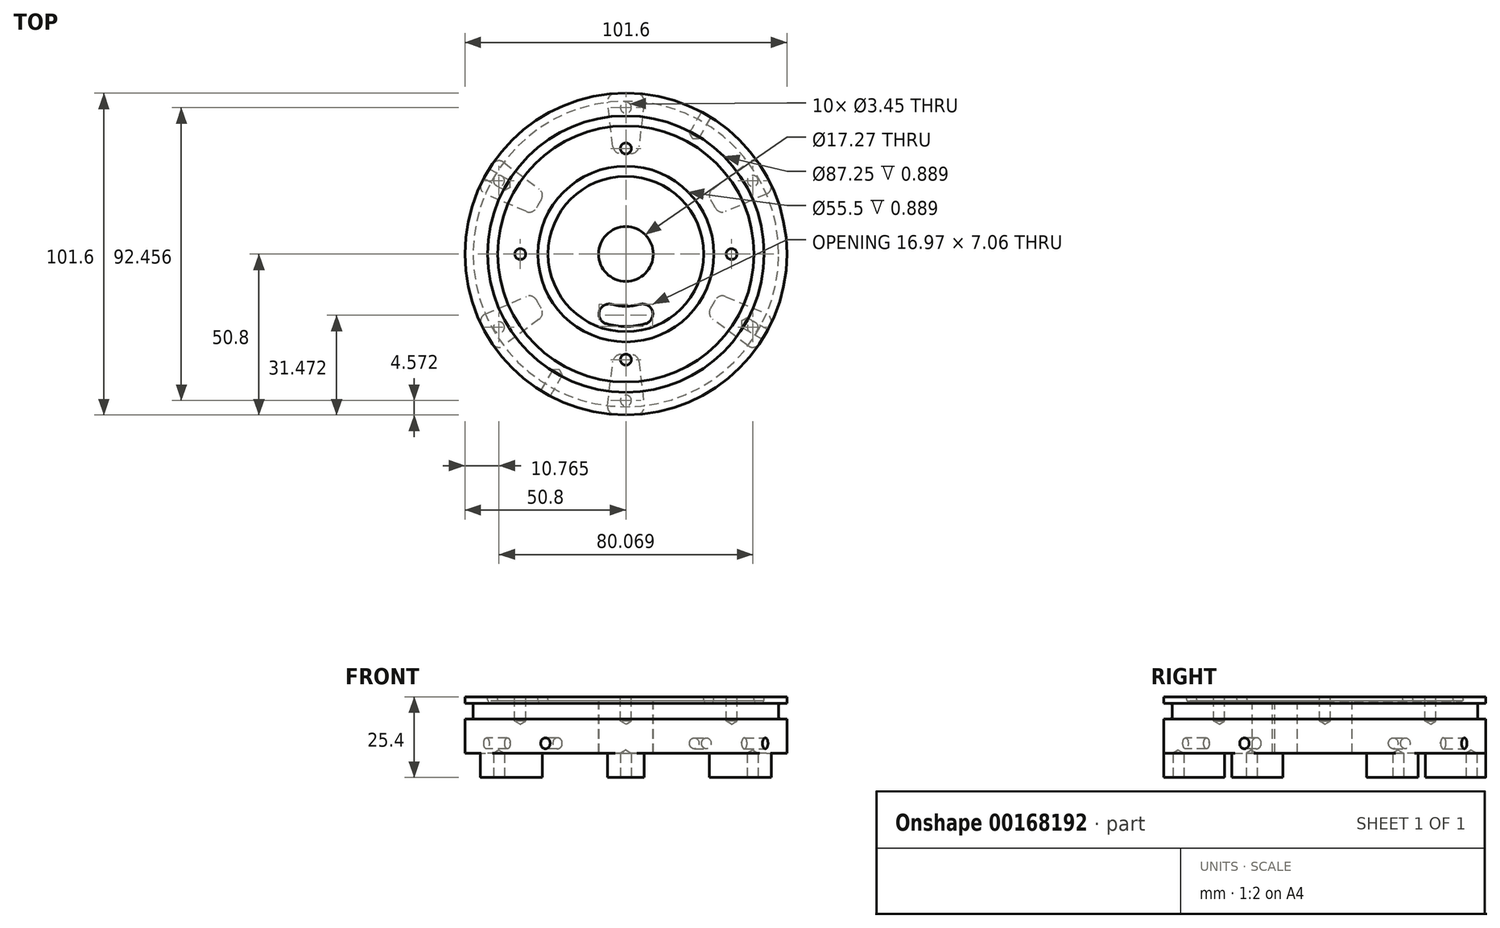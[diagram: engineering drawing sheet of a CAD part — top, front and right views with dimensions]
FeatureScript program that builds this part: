
annotation { "Feature Type Name" : "Feature", "Feature Type Description" : "" }
export const myFeature = defineFeature(function(context is Context, id is Id, definition is map)
    precondition{}
    {
        {
            var Q0;
            Q0=qCreatedBy(makeId("Top.planeOp"),FACE);
            var sketch = newSketch(context, id + "F0", { "sketchPlane" : qUnion([Q0])});
            skCircle(sketch, "E0", {"center": v(0, 0) * mm, "radius": 50.8 * mm});
            skSolve(sketch);
        }
        {
            var Q0;
            Q0=makeQuery(id+"F0.imprint","IMPRINT",FACE,{"disambiguationData":[TD([[makeQuery(id+"F0.imprint","IMPRINT",EDGE,{"derivedFrom":sQuery(id+"F0.wireOp",EDGE,"E0")}),1.0]])]});
            extrude(context, id + "F1", {"entities" : qUnion([Q0]), "depth" : 17.78 * mm});
        }
        {
            var Q0;
            Q0=makeQuery(id+"FNZgXB3MDCEPfWC_1.boolean.opBoolean","SPLIT",FACE,{"disambiguationData":[TD([makeQuery(id+"FNZgXB3MDCEPfWC_1.opExtrude","SWEPT_FACE",FACE,{"disambiguationData":[OSD([sQuery(id+"FiLk9hSRQ8Dv81E_1.wireOp",EDGE,"Xvq2NHEn-EDZK-GzOR-rNrk-moL4fFsD4KvI")])]})])],"derivedFrom":makeQuery(id+"F1.opExtrude","CAP_FACE",FACE,{"disambiguationData":[OSD([sQuery(id+"F0.wireOp",EDGE,"E0")])],"isStart":false})});
            var sketch = newSketch(context, id + "F2", { "sketchPlane" : qUnion([Q0])});
            skCircle(sketch, "E1", {"center": v(0, 0) * mm, "radius": 8.64 * mm});
            skSolve(sketch);
        }
        {
            var Q0;
            Q0=qSketchRegion(id+"F2",true);
            extrude(context, id + "F3", {"entities" : qUnion([Q0]), "operationType" : NewBodyOperationType.REMOVE, "endBound" : BoundingType.THROUGH_ALL, "oppositeDirection" : true, "depth" : 25.4 * mm});
        }
        {
            var Q0;
            Q0=makeQuery(id+"F1.opExtrude","CAP_FACE",FACE,{"disambiguationData":[OSD([sQuery(id+"F0.wireOp",EDGE,"E0")])],"isStart":true});
            var sketch = newSketch(context, id + "F4", { "sketchPlane" : qUnion([Q0])});
            skArc(sketch, "E2", {"start": v(-6.1, -50.43) * mm, "mid": v(0, -50.8) * mm, "end": v(6.1, -50.43) * mm});
            skArc(sketch, "E3", {"start": v(-3.81, -31.52) * mm, "mid": v(0, -31.75) * mm, "end": v(3.8, -31.52) * mm});
            skLineSegment(sketch, "E4", {"start": v(0, 0) * mm, "end": v(3.81, -31.52) * mm, "construction": true});
            skLineSegment(sketch, "E5", {"start": v(6.1, -50.43) * mm, "end": v(3.8, -31.52) * mm});
            skLineSegment(sketch, "E6", {"start": v(-3.8, -31.52) * mm, "end": v(-6.1, -50.43) * mm});
            skLineSegment(sketch, "E7", {"start": v(-3.81, -31.52) * mm, "end": v(3.81, -31.52) * mm, "construction": true});
            skPoint(sketch, "E8", {"position": v(0, -31.52) * mm});
            skLineSegment(sketch, "E9", {"start": v(0, 0) * mm, "end": v(-3.81, -31.52) * mm, "construction": true});
            skSolve(sketch);
        }
        {
            var Q0;
            Q0=qSketchRegion(id+"F4",true);
            extrude(context, id + "F5", {"entities" : qUnion([Q0]), "operationType" : NewBodyOperationType.ADD, "depth" : 7.62 * mm});
        }
        {
            var Q0;
            Q0=makeQuery(id+"F5.opExtrude","SWEPT_EDGE",EDGE,{"disambiguationData":[OSD([sQuery(id+"F0.wireOp",EDGE,"E0"),sQuery(id+"F4.wireOp",EDGE,"E2"),sQuery(id+"F4.wireOp",EDGE,"E5")])]});
            var Q1;
            Q1=makeQuery(id+"F5.opExtrude","SWEPT_EDGE",EDGE,{"disambiguationData":[OSD([sQuery(id+"F4.wireOp",EDGE,"E3"),sQuery(id+"F4.wireOp",EDGE,"E5")])]});
            var Q2;
            Q2=makeQuery(id+"F5.opExtrude","SWEPT_EDGE",EDGE,{"disambiguationData":[OSD([sQuery(id+"F0.wireOp",EDGE,"E0"),sQuery(id+"F4.wireOp",EDGE,"E2"),sQuery(id+"F4.wireOp",EDGE,"sxsrdx0H-xiQs-OsdF-6Z6r-2XBd8uqwUAgb")])]});
            var Q3;
            Q3=makeQuery(id+"F5.opExtrude","SWEPT_EDGE",EDGE,{"disambiguationData":[OSD([sQuery(id+"F4.wireOp",EDGE,"E3"),sQuery(id+"F4.wireOp",EDGE,"sxsrdx0H-xiQs-OsdF-6Z6r-2XBd8uqwUAgb")])]});
            fillet(context, id + "F6", {"entities" : qUnion([Q0, Q1, Q2, Q3]), "radius" : 2.54 * mm, "tangentPropagation" : true, "allowEdgeOverflow" : false});
        }
        {
            var Q0;
            Q0=makeQuery(id+"F5.opExtrude","CAP_FACE",FACE,{"disambiguationData":[OSD([sQuery(id+"F4.wireOp",EDGE,"E2"),sQuery(id+"F4.wireOp",EDGE,"E3"),sQuery(id+"F4.wireOp",EDGE,"E5"),sQuery(id+"F4.wireOp",EDGE,"sxsrdx0H-xiQs-OsdF-6Z6r-2XBd8uqwUAgb")])],"isStart":false});
            var sketch = newSketch(context, id + "F7", { "sketchPlane" : qUnion([Q0])});
            skLineSegment(sketch, "E10", {"start": v(0, 0) * mm, "end": v(0, 0) * mm});
            skLineSegment(sketch, "E11", {"start": v(0, 0) * mm, "end": v(0, -50.68) * mm, "construction": true});
            skPoint(sketch, "E12.3.0", {"position": v(0, -46.23) * mm});
            skPoint(sketch, "E12.center", {"position": v(0, 0) * mm});
            skPoint(sketch, "E13.1.0", {"position": v(40.03, -23.11) * mm});
            skPoint(sketch, "E13.2.0", {"position": v(40.03, 23.11) * mm});
            skPoint(sketch, "E14.0.3.0", {"position": v(0, 46.23) * mm});
            skPoint(sketch, "E14.0.4.0", {"position": v(-40.03, 23.11) * mm});
            skPoint(sketch, "E14.0.5.0", {"position": v(-40.03, -23.11) * mm});
            skSolve(sketch);
        }
        {
            var Q0;
            Q0=makeQuery(id+"F1.opExtrude","SWEPT_BODY",BODY,{"disambiguationData":[OSD([sQuery(id+"F0.wireOp",EDGE,"E0")])]});
            var Q1;
            Q1=makeQuery(id+"F3.boolean.opBoolean","COPY",FACE,{"derivedFrom":makeQuery(id+"F3.opExtrude","SWEPT_FACE",FACE,{"disambiguationData":[OSD([sQuery(id+"F2.wireOp",EDGE,"E1")])]})});
            circularPattern(context, id + "F8", {"operationType" : NewBodyOperationType.ADD, "entities" : qUnion([Q0]), "axis" : qUnion([Q1]), "angle" : 360 * degree, "instanceCount" : 6, "equalSpace" : true});
        }
        {
            var Q0;
            Q0=sQuery(id+"F7.wireOp",VERTEX,"E12.3.0");
            var Q1;
            Q1=sQuery(id+"F7.wireOp",VERTEX,"E13.1.0");
            var Q2;
            Q2=sQuery(id+"F7.wireOp",VERTEX,"E13.2.0");
            var Q3;
            Q3=sQuery(id+"F7.wireOp",VERTEX,"E14.0.3.0");
            var Q4;
            Q4=sQuery(id+"F7.wireOp",VERTEX,"E14.0.4.0");
            var Q5;
            Q5=sQuery(id+"F7.wireOp",VERTEX,"E14.0.5.0");
            var Q6;
            Q6=makeQuery(id+"F1.opExtrude","SWEPT_BODY",BODY,{"disambiguationData":[OSD([sQuery(id+"F0.wireOp",EDGE,"E0")])]});
            hole(context, id + "F9", {"style" : HoleStyle.SIMPLE, "endStyle" : HoleEndStyle.BLIND, "standardTappedOrClearance" : lookupTablePath({ "standard" : "ANSI", "engagement" : "75%", "pitch" : "32 tpi", "size" : "#8", "type" : "Tapped" }), "standardBlindInLast" : lookupTablePath({ "standard" : "ANSI", "engagement" : "75%", "pitch" : "32 tpi", "size" : "#8", "type" : "Tapped" }), "holeDiameter" : 3.45 * mm, "holeDepth" : 7.62 * mm, "locations" : qUnion([Q0, Q1, Q2, Q3, Q4, Q5]), "scope" : qUnion([Q6]), "majorDiameter" : 4.17 * mm});
        }
        {
            var Q0;
            {var subQ0=sQuery(id+"F0.wireOp",EDGE,"E0");Q0=makeQuery(id+"FNZgXB3MDCEPfWC_1.boolean.opBoolean","SPLIT",FACE,{"disambiguationData":[TD([makeQuery(id+"F1.opExtrude","SWEPT_FACE",FACE,{"disambiguationData":[OSD([subQ0])]})])],"derivedFrom":makeQuery(id+"F1.opExtrude","CAP_FACE",FACE,{"disambiguationData":[OSD([subQ0])],"isStart":false})});}
            var sketch = newSketch(context, id + "F10", { "sketchPlane" : qUnion([Q0])});
            skCircle(sketch, "E15", {"center": v(0, 0) * mm, "radius": 42.02 * mm, "construction": true});
            skCircle(sketch, "E16", {"center": v(0, 0) * mm, "radius": 40.42 * mm});
            skCircle(sketch, "E17", {"center": v(0, 0) * mm, "radius": 43.62 * mm});
            skSolve(sketch);
        }
        {
            var Q0;
            Q0=qSketchRegion(id+"F10",true);
            extrude(context, id + "F11", {"entities" : qUnion([Q0]), "operationType" : NewBodyOperationType.REMOVE, "oppositeDirection" : true, "depth" : 1.3 * mm});
        }
        {
            var Q0;
            Q0=makeQuery(id+"F11.boolean.opBoolean","COPY",EDGE,{"derivedFrom":makeQuery(id+"F11.opExtrude","CAP_EDGE",EDGE,{"disambiguationData":[OSD([sQuery(id+"F10.wireOp",EDGE,"E17")])],"isStart":false})});
            var Q1;
            Q1=makeQuery(id+"F11.boolean.opBoolean","COPY",EDGE,{"derivedFrom":makeQuery(id+"F11.opExtrude","CAP_EDGE",EDGE,{"disambiguationData":[OSD([sQuery(id+"F10.wireOp",EDGE,"E16")])],"isStart":false})});
            fillet(context, id + "F12", {"entities" : qUnion([Q0, Q1]), "radius" : 0.4 * mm, "tangentPropagation" : true, "allowEdgeOverflow" : false});
        }
        {
            var Q0;
            Q0=makeQuery(id+"F11.boolean.opBoolean","SPLIT",FACE,{"disambiguationData":[TD([makeQuery(id+"F3.boolean.opBoolean","COPY",FACE,{"derivedFrom":makeQuery(id+"F3.opExtrude","SWEPT_FACE",FACE,{"disambiguationData":[OSD([sQuery(id+"F2.wireOp",EDGE,"E1")])]})})])],"derivedFrom":makeQuery(id+"F1.opExtrude","CAP_FACE",FACE,{"disambiguationData":[OSD([sQuery(id+"F0.wireOp",EDGE,"E0")])],"isStart":false})});
            var sketch = newSketch(context, id + "F13", { "sketchPlane" : qUnion([Q0])});
            skCircle(sketch, "E18", {"center": v(0, 0) * mm, "radius": 26.15 * mm, "construction": true});
            skCircle(sketch, "E19", {"center": v(0, 0) * mm, "radius": 24.55 * mm});
            skCircle(sketch, "E20", {"center": v(0, 0) * mm, "radius": 27.75 * mm});
            skSolve(sketch);
        }
        {
            var Q0;
            Q0=qSketchRegion(id+"F13",true);
            extrude(context, id + "F14", {"entities" : qUnion([Q0]), "operationType" : NewBodyOperationType.REMOVE, "oppositeDirection" : true, "depth" : 1.3 * mm});
        }
        {
            var Q0;
            Q0=makeQuery(id+"F14.boolean.opBoolean","COPY",EDGE,{"derivedFrom":makeQuery(id+"F14.opExtrude","CAP_EDGE",EDGE,{"disambiguationData":[OSD([sQuery(id+"F13.wireOp",EDGE,"E20")])],"isStart":false})});
            var Q1;
            Q1=makeQuery(id+"F14.boolean.opBoolean","COPY",EDGE,{"derivedFrom":makeQuery(id+"F14.opExtrude","CAP_EDGE",EDGE,{"disambiguationData":[OSD([sQuery(id+"F13.wireOp",EDGE,"E19")])],"isStart":false})});
            fillet(context, id + "F15", {"entities" : qUnion([Q0, Q1]), "radius" : 0.4 * mm, "tangentPropagation" : true, "allowEdgeOverflow" : false});
        }
        {
            var Q0;
            {var subQ0=makeQuery(id+"F3.boolean.opBoolean","COPY",FACE,{"derivedFrom":makeQuery(id+"F3.opExtrude","SWEPT_FACE",FACE,{"disambiguationData":[OSD([sQuery(id+"F2.wireOp",EDGE,"E1")])]})});Q0=makeQuery(id+"F14.boolean.opBoolean","SPLIT",FACE,{"disambiguationData":[TD([subQ0])],"derivedFrom":makeQuery(id+"F11.boolean.opBoolean","SPLIT",FACE,{"disambiguationData":[TD([subQ0])],"derivedFrom":makeQuery(id+"F1.opExtrude","CAP_FACE",FACE,{"disambiguationData":[OSD([sQuery(id+"F0.wireOp",EDGE,"E0")])],"isStart":false})})});}
            var sketch = newSketch(context, id + "F16", { "sketchPlane" : qUnion([Q0])});
            skLineSegment(sketch, "E21", {"start": v(0, 0) * mm, "end": v(6.98, -14.96) * mm, "construction": true});
            skArc(sketch, "E22", {"start": v(6.98, -14.96) * mm, "mid": v(0, -16.51) * mm, "end": v(-6.98, -14.96) * mm});
            skArc(sketch, "E23", {"start": v(9.66, -20.72) * mm, "mid": v(0, -22.86) * mm, "end": v(-9.66, -20.72) * mm});
            skLineSegment(sketch, "E24", {"start": v(-9.66, -20.72) * mm, "end": v(-6.98, -14.96) * mm});
            skLineSegment(sketch, "E25", {"start": v(0, 0) * mm, "end": v(-6.98, -14.96) * mm, "construction": true});
            skLineSegment(sketch, "E26", {"start": v(9.66, -20.72) * mm, "end": v(6.98, -14.96) * mm});
            skLineSegment(sketch, "E27", {"start": v(0, -16.51) * mm, "end": v(0, 0) * mm, "construction": true});
            skSolve(sketch);
        }
        {
            var Q0;
            Q0=qSketchRegion(id+"F16",true);
            extrude(context, id + "F17", {"entities" : qUnion([Q0]), "operationType" : NewBodyOperationType.REMOVE, "endBound" : BoundingType.THROUGH_ALL, "oppositeDirection" : true, "depth" : 25.4 * mm});
        }
        {
            var Q0;
            Q0=makeQuery(id+"F17.boolean.opBoolean","COPY",EDGE,{"derivedFrom":makeQuery(id+"F17.opExtrude","SWEPT_EDGE",EDGE,{"disambiguationData":[OSD([sQuery(id+"F16.wireOp",EDGE,"E22"),sQuery(id+"F16.wireOp",EDGE,"E24")])]})});
            var Q1;
            Q1=makeQuery(id+"F17.boolean.opBoolean","COPY",EDGE,{"derivedFrom":makeQuery(id+"F17.opExtrude","SWEPT_EDGE",EDGE,{"disambiguationData":[OSD([sQuery(id+"F16.wireOp",EDGE,"E23"),sQuery(id+"F16.wireOp",EDGE,"E24")])]})});
            var Q2;
            Q2=makeQuery(id+"F17.boolean.opBoolean","COPY",EDGE,{"derivedFrom":makeQuery(id+"F17.opExtrude","SWEPT_EDGE",EDGE,{"disambiguationData":[OSD([sQuery(id+"F16.wireOp",EDGE,"E22"),sQuery(id+"F16.wireOp",EDGE,"nJm0js4g-YAOA-XNub-Ppl5-B8IrQimasCNu")])]})});
            var Q3;
            Q3=makeQuery(id+"F17.boolean.opBoolean","COPY",EDGE,{"derivedFrom":makeQuery(id+"F17.opExtrude","SWEPT_EDGE",EDGE,{"disambiguationData":[OSD([sQuery(id+"F16.wireOp",EDGE,"E23"),sQuery(id+"F16.wireOp",EDGE,"nJm0js4g-YAOA-XNub-Ppl5-B8IrQimasCNu")])]})});
            fillet(context, id + "F18", {"entities" : qUnion([Q0, Q1, Q2, Q3]), "radius" : 3.17 * mm, "tangentPropagation" : true, "allowEdgeOverflow" : false});
        }
        {
            var Q0;
            {var subQ0=makeQuery(id+"F11.opExtrude","SWEPT_FACE",FACE,{"disambiguationData":[OSD([sQuery(id+"F10.wireOp",EDGE,"E16")])]});Q0=makeQuery(id+"F14.boolean.opBoolean","SPLIT",FACE,{"disambiguationData":[TD([makeQuery(id+"F11.boolean.opBoolean","COPY",FACE,{"derivedFrom":subQ0})])],"derivedFrom":makeQuery(id+"F11.boolean.opBoolean","SPLIT",FACE,{"disambiguationData":[TD([makeQuery(id+"F3.boolean.opBoolean","COPY",FACE,{"derivedFrom":makeQuery(id+"F3.opExtrude","SWEPT_FACE",FACE,{"disambiguationData":[OSD([sQuery(id+"F2.wireOp",EDGE,"E1")])]})})])],"derivedFrom":makeQuery(id+"F1.opExtrude","CAP_FACE",FACE,{"disambiguationData":[OSD([sQuery(id+"F0.wireOp",EDGE,"E0")])],"isStart":false})})});}
            var sketch = newSketch(context, id + "F19", { "sketchPlane" : qUnion([Q0])});
            skCircle(sketch, "E28", {"center": v(0, 0) * mm, "radius": 33.34 * mm, "construction": true});
            skLineSegment(sketch, "E29", {"start": v(0, 0) * mm, "end": v(0, -33.34) * mm, "construction": true});
            skPoint(sketch, "E30", {"position": v(0, -33.34) * mm});
            skPoint(sketch, "E31", {"position": v(-33.34, 0) * mm});
            skPoint(sketch, "E32", {"position": v(33.34, 0) * mm});
            skPoint(sketch, "E33", {"position": v(0, 33.34) * mm});
            skSolve(sketch);
        }
        {
            var Q0;
            {var subQ1=sQuery(id+"F0.wireOp",EDGE,"E0");var subQ2=makeQuery(id+"F1.opExtrude","SWEPT_FACE",FACE,{"disambiguationData":[OSD([subQ1])]});Q0=makeQuery(id+"F11.boolean.opBoolean","SPLIT",FACE,{"disambiguationData":[TD([subQ2])],"derivedFrom":makeQuery(id+"F1.opExtrude","CAP_FACE",FACE,{"disambiguationData":[OSD([subQ1])],"isStart":false})});}
            cPlane(context, id + "F20", {"entities" : qUnion([Q0]), "cplaneType" : CPlaneType.OFFSET, "offset" : 2.03 * mm, "oppositeDirection" : true, "width" : 152.4 * mm, "height" : 152.4 * mm});
        }
        {
            var Q0;
            Q0=qCreatedBy(id+"F20.planeOp",FACE);
            var sketch = newSketch(context, id + "F21", { "sketchPlane" : qUnion([Q0])});
            skCircle(sketch, "E34", {"center": v(0, 0) * mm, "radius": 48.2 * mm});
            skCircle(sketch, "E35.0", {"center": v(0, 0) * mm, "radius": 50.8 * mm});
            skSolve(sketch);
        }
        {
            var Q0;
            Q0=qSketchRegion(id+"F21",true);
            extrude(context, id + "F22", {"entities" : qUnion([Q0]), "operationType" : NewBodyOperationType.REMOVE, "oppositeDirection" : true, "depth" : 5 * mm});
        }
        {
            var Q0;
            Q0=makeQuery(id+"F22.boolean.opBoolean","COPY",EDGE,{"derivedFrom":makeQuery(id+"F22.opExtrude","CAP_EDGE",EDGE,{"disambiguationData":[OSD([sQuery(id+"F21.wireOp",EDGE,"E34")])],"isStart":false})});
            var Q1;
            Q1=makeQuery(id+"F22.boolean.opBoolean","COPY",EDGE,{"derivedFrom":makeQuery(id+"F22.opExtrude","CAP_EDGE",EDGE,{"disambiguationData":[OSD([sQuery(id+"F21.wireOp",EDGE,"E34")])],"isStart":true})});
            fillet(context, id + "F23", {"entities" : qUnion([Q0, Q1]), "radius" : 0.76 * mm, "tangentPropagation" : true, "allowEdgeOverflow" : false});
        }
        {
            var Q0;
            {var subQ1=sQuery(id+"F0.wireOp",EDGE,"E0");var subQ2=makeQuery(id+"F1.opExtrude","SWEPT_FACE",FACE,{"disambiguationData":[OSD([subQ1])]});Q0=makeQuery(id+"F11.boolean.opBoolean","SPLIT",FACE,{"disambiguationData":[TD([subQ2])],"derivedFrom":makeQuery(id+"F1.opExtrude","CAP_FACE",FACE,{"disambiguationData":[OSD([subQ1])],"isStart":false})});}
            var sketch = newSketch(context, id + "F24", { "sketchPlane" : qUnion([Q0])});
            skCircle(sketch, "E36.0", {"center": v(0, 0) * mm, "radius": 50.8 * mm, "construction": true});
            skPoint(sketch, "E37", {"position": v(-25.4, -44) * mm});
            skLineSegment(sketch, "E38", {"start": v(0, -50.8) * mm, "end": v(0, 0) * mm, "construction": true});
            skLineSegment(sketch, "E39", {"start": v(0, 0) * mm, "end": v(-17.96, -31.1) * mm, "construction": true});
            skLineSegment(sketch, "E40", {"start": v(-17.96, -31.1) * mm, "end": v(-25.4, -44) * mm, "construction": true});
            skLineSegment(sketch, "E41", {"start": v(0, 0) * mm, "end": v(25.4, 44) * mm, "construction": true});
            skLineSegment(sketch, "E42", {"start": v(25.4, 44) * mm, "end": v(0, 0) * mm, "construction": true});
            skLineSegment(sketch, "E43", {"start": v(44, -25.4) * mm, "end": v(0, 0) * mm, "construction": true});
            skLineSegment(sketch, "E44", {"start": v(0, 0) * mm, "end": v(-44, 25.4) * mm, "construction": true});
            skPoint(sketch, "E45", {"position": v(25.4, 44) * mm});
            skPoint(sketch, "E46", {"position": v(44, -25.4) * mm});
            skPoint(sketch, "E47", {"position": v(-44, 25.4) * mm});
            skSolve(sketch);
        }
        {
            var Q0;
            Q0=qCreatedBy(makeId("Front.planeOp"),FACE);
            var sketch = newSketch(context, id + "F25", { "sketchPlane" : qUnion([Q0])});
            skLineSegment(sketch, "E48", {"start": v(0, 0) * mm, "end": v(0, 38.57) * mm, "construction": true});
            skSolve(sketch);
        }
        {
            var Q0;
            Q0=sQuery(id+"F25.wireOp",EDGE,"E48");
            cPlane(context, id + "F26", {"entities" : qUnion([Q0]), "cplaneType" : CPlaneType.LINE_ANGLE, "offset" : 25.4 * mm, "angle" : 60 * degree, "width" : 152.4 * mm, "height" : 152.4 * mm});
        }
        {
            var Q0;
            Q0=sQuery(id+"F24.wireOp",VERTEX,"E37");
            var Q1;
            Q1=qCreatedBy(id+"F26.planeOp",FACE);
            cPlane(context, id + "F27", {"entities" : qUnion([Q0, Q1]), "cplaneType" : CPlaneType.PLANE_POINT, "offset" : 25.4 * mm, "width" : 152.4 * mm, "height" : 152.4 * mm});
        }
        {
            var Q0;
            Q0=qCreatedBy(id+"F27.planeOp",FACE);
            var Q1;
            Q1=sQuery(id+"F24.wireOp",VERTEX,"E45");
            cPlane(context, id + "F28", {"entities" : qUnion([Q0, Q1]), "cplaneType" : CPlaneType.PLANE_POINT, "offset" : 25.4 * mm, "width" : 152.4 * mm, "height" : 152.4 * mm});
        }
        {
            var Q0;
            Q0=sQuery(id+"F25.wireOp",EDGE,"E48");
            cPlane(context, id + "F29", {"entities" : qUnion([Q0]), "cplaneType" : CPlaneType.LINE_ANGLE, "offset" : 25.4 * mm, "angle" : 150 * degree, "width" : 152.4 * mm, "height" : 152.4 * mm});
        }
        {
            var Q0;
            Q0=sQuery(id+"F24.wireOp",VERTEX,"E47");
            var Q1;
            Q1=qCreatedBy(id+"F29.planeOp",FACE);
            cPlane(context, id + "F30", {"entities" : qUnion([Q0, Q1]), "cplaneType" : CPlaneType.PLANE_POINT, "offset" : 25.4 * mm, "width" : 152.4 * mm, "height" : 152.4 * mm});
        }
        {
            var Q0;
            Q0=qCreatedBy(id+"F29.planeOp",FACE);
            var Q1;
            Q1=sQuery(id+"F24.wireOp",VERTEX,"E46");
            cPlane(context, id + "F31", {"entities" : qUnion([Q0, Q1]), "cplaneType" : CPlaneType.PLANE_POINT, "offset" : 25.4 * mm, "width" : 152.4 * mm, "height" : 152.4 * mm});
        }
        {
            var Q0;
            Q0=qCreatedBy(id+"F27.planeOp",FACE);
            var sketch = newSketch(context, id + "F32", { "sketchPlane" : qUnion([Q0])});
            skLineSegment(sketch, "E49", {"start": v(0, 0) * mm, "end": v(0, 3.12) * mm, "construction": true});
            skPoint(sketch, "E50", {"position": v(0, 3.12) * mm});
            skSolve(sketch);
        }
        {
            var Q0;
            Q0=qCreatedBy(id+"F28.planeOp",FACE);
            var sketch = newSketch(context, id + "F33", { "sketchPlane" : qUnion([Q0])});
            skPoint(sketch, "E51", {"position": v(0, 3.12) * mm});
            skLineSegment(sketch, "E52.0", {"start": v(0, 0) * mm, "end": v(0, 3.12) * mm, "construction": true});
            skSolve(sketch);
        }
        {
            var Q0;
            Q0=qCreatedBy(id+"F30.planeOp",FACE);
            var sketch = newSketch(context, id + "F34", { "sketchPlane" : qUnion([Q0])});
            skLineSegment(sketch, "E53", {"start": v(0, 0) * mm, "end": v(0, 3.12) * mm, "construction": true});
            skLineSegment(sketch, "E54.0", {"start": v(-50.8, 0) * mm, "end": v(-50.8, 3.12) * mm, "construction": true});
            skPoint(sketch, "E55", {"position": v(0, 3.12) * mm});
            skLineSegment(sketch, "E56", {"start": v(-50.8, 3.12) * mm, "end": v(0, 3.12) * mm, "construction": true});
            skSolve(sketch);
        }
        {
            var Q0;
            Q0=qCreatedBy(id+"F31.planeOp",FACE);
            var sketch = newSketch(context, id + "F35", { "sketchPlane" : qUnion([Q0])});
            skLineSegment(sketch, "E57.0", {"start": v(0, 0) * mm, "end": v(0, 3.12) * mm, "construction": true});
            skPoint(sketch, "E58", {"position": v(0, 3.12) * mm});
            skSolve(sketch);
        }
        {
            var Q0;
            Q0=sQuery(id+"F35.wireOp",VERTEX,"E58");
            var Q1;
            Q1=makeQuery(id+"F1.opExtrude","SWEPT_BODY",BODY,{"disambiguationData":[OSD([sQuery(id+"F0.wireOp",EDGE,"E0")])]});
            hole(context, id + "F36", {"style" : HoleStyle.SIMPLE, "endStyle" : HoleEndStyle.BLIND, "oppositeDirection" : true, "standardTappedOrClearance" : lookupTablePath({ "standard" : "ANSI", "engagement" : "75%", "pitch" : "32 tpi", "size" : "#8", "type" : "Tapped" }), "standardBlindInLast" : lookupTablePath({ "standard" : "ANSI", "engagement" : "75%", "pitch" : "32 tpi", "size" : "#8", "type" : "Tapped" }), "holeDiameter" : 3.45 * mm, "holeDepth" : 7.62 * mm, "locations" : qUnion([Q0]), "scope" : qUnion([Q1]), "majorDiameter" : 4.17 * mm});
        }
        {
            var Q0;
            Q0=sQuery(id+"F34.wireOp",VERTEX,"E55");
            var Q1;
            Q1=makeQuery(id+"F1.opExtrude","SWEPT_BODY",BODY,{"disambiguationData":[OSD([sQuery(id+"F0.wireOp",EDGE,"E0")])]});
            hole(context, id + "F37", {"style" : HoleStyle.SIMPLE, "endStyle" : HoleEndStyle.BLIND, "standardTappedOrClearance" : lookupTablePath({ "standard" : "ANSI", "engagement" : "75%", "pitch" : "32 tpi", "size" : "#8", "type" : "Tapped" }), "standardBlindInLast" : lookupTablePath({ "standard" : "ANSI", "engagement" : "75%", "pitch" : "32 tpi", "size" : "#8", "type" : "Tapped" }), "holeDiameter" : 3.45 * mm, "holeDepth" : 7.62 * mm, "locations" : qUnion([Q0]), "scope" : qUnion([Q1]), "majorDiameter" : 4.17 * mm});
        }
        {
            var Q0;
            Q0=sQuery(id+"F32.wireOp",VERTEX,"E50");
            var Q1;
            Q1=makeQuery(id+"F1.opExtrude","SWEPT_BODY",BODY,{"disambiguationData":[OSD([sQuery(id+"F0.wireOp",EDGE,"E0")])]});
            hole(context, id + "F38", {"style" : HoleStyle.SIMPLE, "endStyle" : HoleEndStyle.BLIND, "oppositeDirection" : true, "standardTappedOrClearance" : lookupTablePath({ "standard" : "ANSI", "engagement" : "75%", "pitch" : "32 tpi", "size" : "#8", "type" : "Tapped" }), "standardBlindInLast" : lookupTablePath({ "standard" : "ANSI", "engagement" : "75%", "pitch" : "32 tpi", "size" : "#8", "type" : "Tapped" }), "holeDiameter" : 3.45 * mm, "holeDepth" : 7.62 * mm, "locations" : qUnion([Q0]), "scope" : qUnion([Q1]), "majorDiameter" : 4.17 * mm});
        }
        {
            var Q0;
            Q0=sQuery(id+"F33.wireOp",VERTEX,"E51");
            var Q1;
            Q1=makeQuery(id+"F1.opExtrude","SWEPT_BODY",BODY,{"disambiguationData":[OSD([sQuery(id+"F0.wireOp",EDGE,"E0")])]});
            hole(context, id + "F39", {"style" : HoleStyle.SIMPLE, "endStyle" : HoleEndStyle.BLIND, "standardTappedOrClearance" : lookupTablePath({ "standard" : "ANSI", "engagement" : "75%", "pitch" : "32 tpi", "size" : "#8", "type" : "Tapped" }), "standardBlindInLast" : lookupTablePath({ "standard" : "ANSI", "engagement" : "75%", "pitch" : "32 tpi", "size" : "#8", "type" : "Tapped" }), "holeDiameter" : 3.45 * mm, "holeDepth" : 7.62 * mm, "locations" : qUnion([Q0]), "scope" : qUnion([Q1]), "majorDiameter" : 4.17 * mm});
        }
        {
            var Q0;
            Q0=sQuery(id+"F19.wireOp",VERTEX,"E31");
            var Q1;
            Q1=sQuery(id+"F19.wireOp",VERTEX,"E33");
            var Q2;
            Q2=sQuery(id+"F19.wireOp",VERTEX,"E32");
            var Q3;
            Q3=sQuery(id+"F19.wireOp",VERTEX,"E30");
            var Q4;
            Q4=makeQuery(id+"F1.opExtrude","SWEPT_BODY",BODY,{"disambiguationData":[OSD([sQuery(id+"F0.wireOp",EDGE,"E0")])]});
            hole(context, id + "F40", {"style" : HoleStyle.SIMPLE, "endStyle" : HoleEndStyle.BLIND, "standardTappedOrClearance" : lookupTablePath({ "standard" : "ANSI", "engagement" : "75%", "pitch" : "32 tpi", "size" : "#8", "type" : "Tapped" }), "standardBlindInLast" : lookupTablePath({ "standard" : "ANSI", "engagement" : "75%", "pitch" : "32 tpi", "size" : "#8", "type" : "Tapped" }), "holeDiameter" : 3.45 * mm, "holeDepth" : 7.62 * mm, "locations" : qUnion([Q0, Q1, Q2, Q3]), "scope" : qUnion([Q4]), "majorDiameter" : 4.17 * mm});
        }
    });
